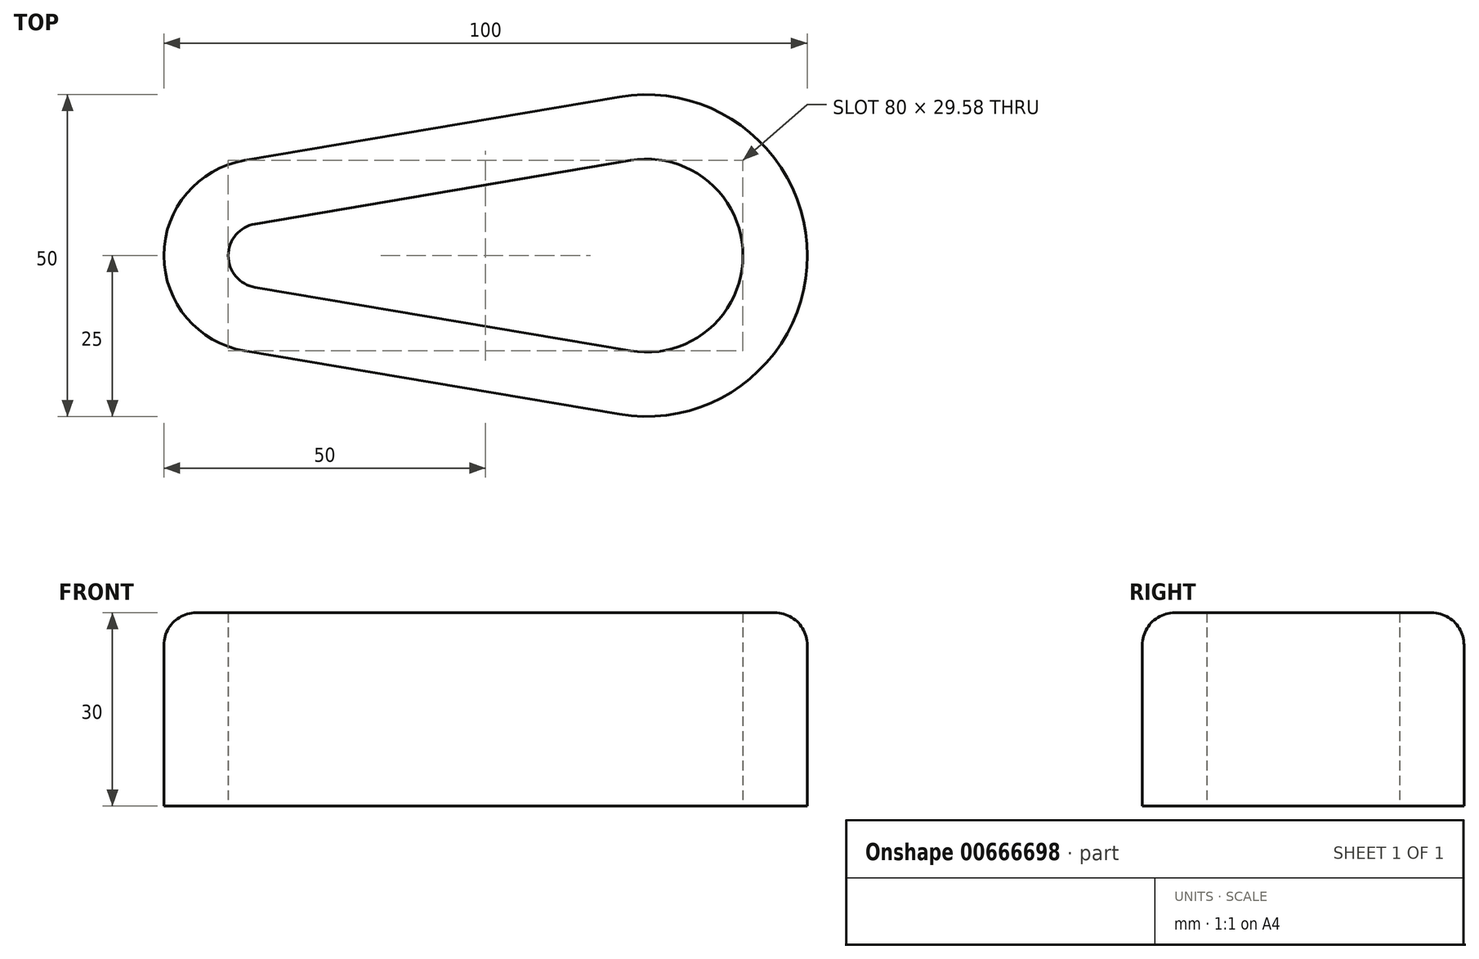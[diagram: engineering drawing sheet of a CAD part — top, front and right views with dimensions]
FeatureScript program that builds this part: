
annotation { "Feature Type Name" : "Feature", "Feature Type Description" : "" }
export const myFeature = defineFeature(function(context is Context, id is Id, definition is map)
    precondition{}
    {
        {
            var Q0;
            Q0=qCreatedBy(makeId("Top.planeOp"),FACE);
            var sketch = newSketch(context, id + "F0", { "sketchPlane" : qUnion([Q0])});
            skArc(sketch, "E0", {"start": v(-2.5, 14.8) * mm, "mid": v(-15, 0) * mm, "end": v(-2.5, -14.8) * mm});
            skArc(sketch, "E1", {"start": v(55.83, -24.65) * mm, "mid": v(85, 0) * mm, "end": v(55.83, 24.65) * mm});
            skLineSegment(sketch, "E2", {"start": v(-2.5, 14.8) * mm, "end": v(55.83, 24.65) * mm});
            skLineSegment(sketch, "E3", {"start": v(0, 0) * mm, "end": v(60, 0) * mm, "construction": true});
            skLineSegment(sketch, "E4.MirrorCS", {"start": v(-2.5, -14.8) * mm, "end": v(55.83, -24.65) * mm});
            skLineSegment(sketch, "E5.0", {"start": v(-0.83, 4.93) * mm, "end": v(57.5, 14.8) * mm});
            skArc(sketch, "E5.1", {"start": v(-0.83, 4.93) * mm, "mid": v(-5, 0) * mm, "end": v(-0.83, -4.93) * mm});
            skLineSegment(sketch, "E5.2", {"start": v(-0.83, -4.93) * mm, "end": v(57.5, -14.8) * mm});
            skArc(sketch, "E5.3", {"start": v(57.5, -14.8) * mm, "mid": v(75, 0) * mm, "end": v(57.5, 14.8) * mm});
            skSolve(sketch);
        }
        {
            var Q0;
            Q0 = qSketchRegion(id + "F0", true);
            extrude(context, id + "F1", {"entities" : qUnion([Q0]), "depth" : 30 * mm, "offsetDistance" : 25 * mm});
        }
        {
            var Q0;
            Q0=makeQuery(id+"F1.opExtrude","CAP_EDGE",EDGE,{"disambiguationData":[OSD([sQuery(id+"F0.wireOp",EDGE,"E0")])],"isStart":false});
            var Q1;
            Q1=makeQuery(id+"F1.opExtrude","CAP_EDGE",EDGE,{"disambiguationData":[OSD([sQuery(id+"F0.wireOp",EDGE,"E4.MirrorCS")])],"isStart":false});
            var Q2;
            Q2=makeQuery(id+"F1.opExtrude","CAP_EDGE",EDGE,{"disambiguationData":[OSD([sQuery(id+"F0.wireOp",EDGE,"E1")])],"isStart":false});
            var Q3;
            Q3=makeQuery(id+"F1.opExtrude","CAP_EDGE",EDGE,{"disambiguationData":[OSD([sQuery(id+"F0.wireOp",EDGE,"E2")])],"isStart":false});
            fillet(context, id + "F2", {"entities" : qUnion([Q0, Q1, Q2, Q3]), "radius" : 5 * mm, "tangentPropagation" : true, "allowEdgeOverflow" : false});
        }
    });
